# Revit family: Door_Swing Door_The Sliding Door Company_Single Door with Column Beam & Transom_3 Fixed Panel
name_source: partatom
category: Doors
units: mm (PartAtom-declared; Revit-internal decimal feet)

## family parameters
Always vertical = Yes
Cut with Voids When Loaded = No
Host = Wall
OmniClass Number = 23.30.10.00
OmniClass Title = Doors
Room Calculation Point = No
Shared = No

## types (1)
- Single Swing Door with Transom & 3 Fixed Panel
    ADA Opening Clearance = Minimum of 32 inches Opening Clearance
    Beam = 2"
    Column & Beam Sizes = Available Only in 2x4 & 4x4 Sizes
    Column at Handle Side = 2"
    Column at Hinge Side = 2"
    Description = Swing Door with Column & Beam + Transom + 3 Fixed Panel
    FP 1 1/2" Frame (No Support Dividers) = Max. H=108 in. Max. W=50 in. panel width
    FP 3" Frame (No Support Dividers) = Max. H=122 in. Max. W=52 in. panel width
    FP Glass Limitation = Panel Width x System Height cannot exceed 7,400 square inches
    FP Order Height = 96"
    FP Order Width = 100"
    FP Panel Height = 94 1/2"
    FP Panel Width = 32 5/8"
    FP Stile/Rail = 3"
    Finished Opening Height = 120"
    Finished Opening Width = 140"
    Frame Projection Ext. = 1"
    Frame Projection Int. = 1"
    Frame Width = 3"
    Function = Interior
    Height = 96"
    Manufacturer = The Sliding Door Company
    Maximum Door Panel Height = 108 inches
    Maximum Door Panel Width = 40 inches
    Maximum Door Swing = 120 degress
    Maximum Transom Order Height = 48 inches
    Model = Swing Door with Column & Beam + Transom + 3 Fixed Panel
    Overall System Height = 120"
    Overall System Width = 140"
    PULL = No
    PUSH = Yes
    Pull Kickplate = No
    Pull Lever Set = No
    Pull Round Designer Handle 12" = No
    Push Kickplate = Yes
    Push Lever Set = Yes
    Push Round Designer Handle 12" = No
    SD Bottom Side Gap = 5/8"
    SD Handle Side Gap = 1/8"
    SD Hinge Side Gap = 1/4"
    SD Opening Clearance Height = 95 1/2"
    SD Opening Clearance Width = 33 1/2"
    SD Order Height = 96"
    SD Order Width = 36"
    SD Panel Height = 95 1/8"
    SD Panel Width = 35 5/8"
    SD Stile/Rail = 3"
    SD Top Side Gap = 1/4"
    Thickness = 1 1/4"
    Transom Order Height = 22"
    Transom Order Width = 140"
    Transom Panel Height = 20 1/2"
    Transom Stile/Rail = 1 1/2"
    URL = https://www.slidingdoorco.com
    Wall Closure = By host
    Width = 36"

## geometry (parser evidence)
native form markers: Blend x6, Extrusion x8, Sweep x14
no freeform markers — native parametric forms only
